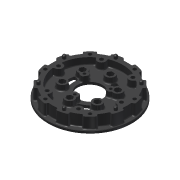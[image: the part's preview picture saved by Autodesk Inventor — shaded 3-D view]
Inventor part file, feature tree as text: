
AUTODESK INVENTOR PART (.ipt)
format: ipt  version: 2013 (Build 170138000, 138)  size: 1,559,552 bytes
history: native  units: in
note: dims shown in document units (in); Inventor stores cm internally (conversion verified against a paired STEP export)
features: fillet x1, other x1, imported_body x1
ambient origin geometry x8: Origin, YZ Plane, XZ Plane, XY Plane, X Axis, Y Axis, Z Axis, Center Point
feature tree (3):
  fillet  "Fillet18"  [1 undecoded]
  other  "217-2588-001 Rev41"
  imported_body  "Base1"
note: 1 required parameter value undecoded (feature->parameter linkage not recoverable at this tier; creation-order binding heuristic only, values carry confidence <= 0.55)
